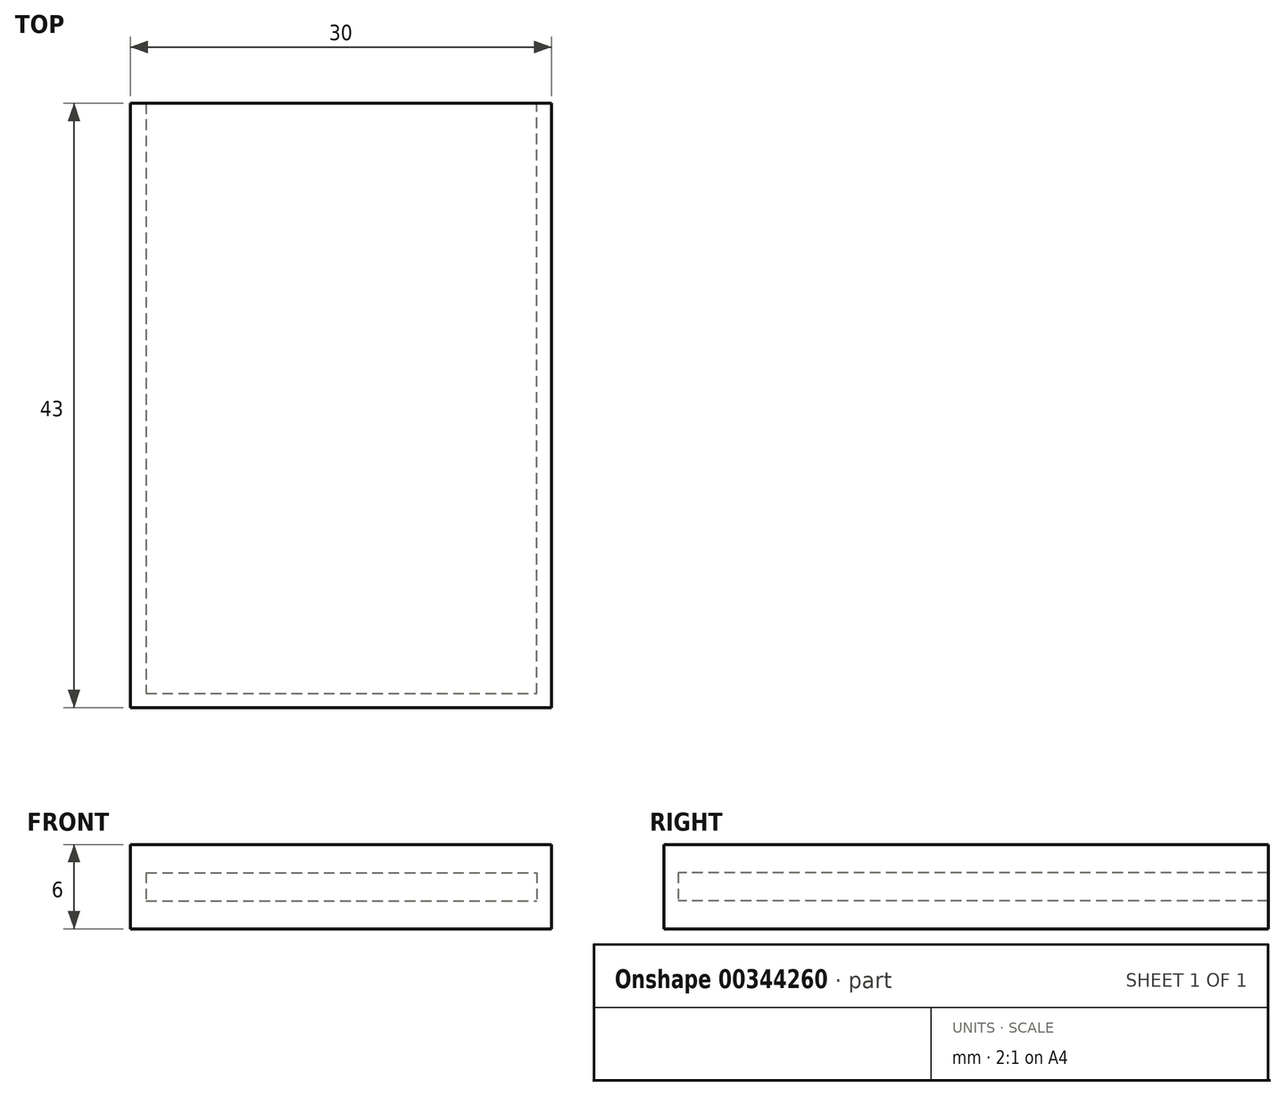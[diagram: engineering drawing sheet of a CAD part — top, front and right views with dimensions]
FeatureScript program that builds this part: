
annotation { "Feature Type Name" : "Feature", "Feature Type Description" : "" }
export const myFeature = defineFeature(function(context is Context, id is Id, definition is map)
    precondition{}
    {
        {
            var Q0;
            Q0=qCreatedBy(makeId("Top.planeOp"),FACE);
            var sketch = newSketch(context, id + "F0", { "sketchPlane" : qUnion([Q0])});
            skLineSegment(sketch, "E0.bottom", {"start": v(-15, 21.5) * mm, "end": v(15, 21.5) * mm});
            skLineSegment(sketch, "E0.top", {"start": v(-15, -21.5) * mm, "end": v(15, -21.5) * mm});
            skLineSegment(sketch, "E0.left", {"start": v(-15, 21.5) * mm, "end": v(-15, -21.5) * mm});
            skLineSegment(sketch, "E0.right", {"start": v(15, 21.5) * mm, "end": v(15, -21.5) * mm});
            skPoint(sketch, "E0.middle", {"position": v(0, 0) * mm});
            skSolve(sketch);
        }
        {
            var Q0;
            Q0 = qSketchRegion(id + "F0", true);
            extrude(context, id + "F1", {"entities" : qUnion([Q0]), "depth" : 2 * mm});
        }
        {
            var Q0;
            Q0=makeQuery(id+"F1.opExtrude","CAP_FACE",FACE,{"disambiguationData":[OSD([sQuery(id+"F0.wireOp",EDGE,"E0.bottom"),sQuery(id+"F0.wireOp",EDGE,"E0.top"),sQuery(id+"F0.wireOp",EDGE,"E0.left"),sQuery(id+"F0.wireOp",EDGE,"E0.right")])],"isStart":false});
            var sketch = newSketch(context, id + "F2", { "sketchPlane" : qUnion([Q0])});
            skLineSegment(sketch, "E1", {"start": v(-13.86, 21.5) * mm, "end": v(-13.86, -20.51) * mm});
            skLineSegment(sketch, "E2", {"start": v(-13.86, -20.51) * mm, "end": v(13.92, -20.51) * mm});
            skLineSegment(sketch, "E3", {"start": v(13.92, -20.51) * mm, "end": v(13.92, 21.5) * mm});
            skSolve(sketch);
        }
        {
            var Q0;
            {var subQ1=sQuery(id+"F2.wireOp",EDGE,"E1");Q0=makeQuery(id+"F2.imprint","IMPRINT",FACE,{"disambiguationData":[TD([[makeQuery(id+"F2.imprint","IMPRINT",EDGE,{"derivedFrom":subQ1}),-1.0]])]});}
            extrude(context, id + "F3", {"entities" : qUnion([Q0]), "operationType" : NewBodyOperationType.ADD, "depth" : 2 * mm});
        }
        {
            var Q0;
            Q0=makeQuery(id+"F3.opExtrude","CAP_FACE",FACE,{"disambiguationData":[OSD([sQuery(id+"F0.wireOp",EDGE,"E0.bottom"),sQuery(id+"F0.wireOp",EDGE,"E0.top"),sQuery(id+"F0.wireOp",EDGE,"E0.left"),sQuery(id+"F0.wireOp",EDGE,"E0.right"),sQuery(id+"F2.wireOp",EDGE,"E1"),sQuery(id+"F2.wireOp",EDGE,"E2"),sQuery(id+"F2.wireOp",EDGE,"E3")])],"isStart":false});
            var sketch = newSketch(context, id + "F4", { "sketchPlane" : qUnion([Q0])});
            skLineSegment(sketch, "E4", {"start": v(-15, 21.5) * mm, "end": v(-15, -21.5) * mm});
            skLineSegment(sketch, "E5", {"start": v(-15, -21.5) * mm, "end": v(15, -21.5) * mm});
            skLineSegment(sketch, "E6", {"start": v(15, -21.5) * mm, "end": v(15, 21.5) * mm});
            skLineSegment(sketch, "E7", {"start": v(15, 21.5) * mm, "end": v(-15, 21.5) * mm});
            skSolve(sketch);
        }
        {
            var Q0;
            Q0 = qSketchRegion(id + "F4", true);
            extrude(context, id + "F5", {"entities" : qUnion([Q0]), "operationType" : NewBodyOperationType.ADD, "depth" : 2 * mm});
        }
    });
